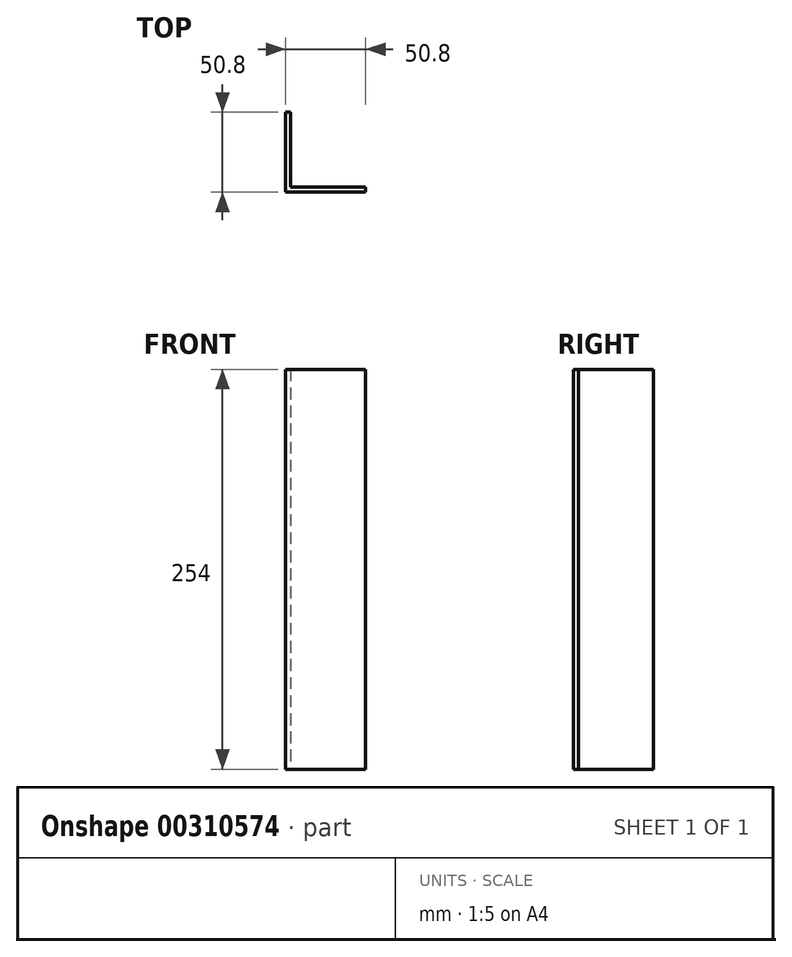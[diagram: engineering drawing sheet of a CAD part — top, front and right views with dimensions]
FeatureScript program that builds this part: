
annotation { "Feature Type Name" : "Feature", "Feature Type Description" : "" }
export const myFeature = defineFeature(function(context is Context, id is Id, definition is map)
    precondition{}
    {
        {
            var Q0;
            Q0=qCreatedBy(makeId("Top.planeOp"),FACE);
            var sketch = newSketch(context, id + "F0", { "sketchPlane" : qUnion([Q0])});
            skLineSegment(sketch, "E0", {"start": v(0, 0) * mm, "end": v(0, 50.8) * mm});
            skLineSegment(sketch, "E1", {"start": v(0, 50.8) * mm, "end": v(3.18, 50.8) * mm});
            skLineSegment(sketch, "E2", {"start": v(3.18, 50.8) * mm, "end": v(3.18, 3.17) * mm});
            skLineSegment(sketch, "E3", {"start": v(3.18, 3.17) * mm, "end": v(50.8, 3.18) * mm});
            skLineSegment(sketch, "E4", {"start": v(50.8, 3.18) * mm, "end": v(50.8, 0) * mm});
            skLineSegment(sketch, "E5", {"start": v(50.8, 0) * mm, "end": v(0, 0) * mm});
            skSolve(sketch);
        }
        {
            var Q0;
            Q0 = qSketchRegion(id + "F0", true);
            extrude(context, id + "F1", {"entities" : qUnion([Q0]), "depth" : 254 * mm});
        }
    });
